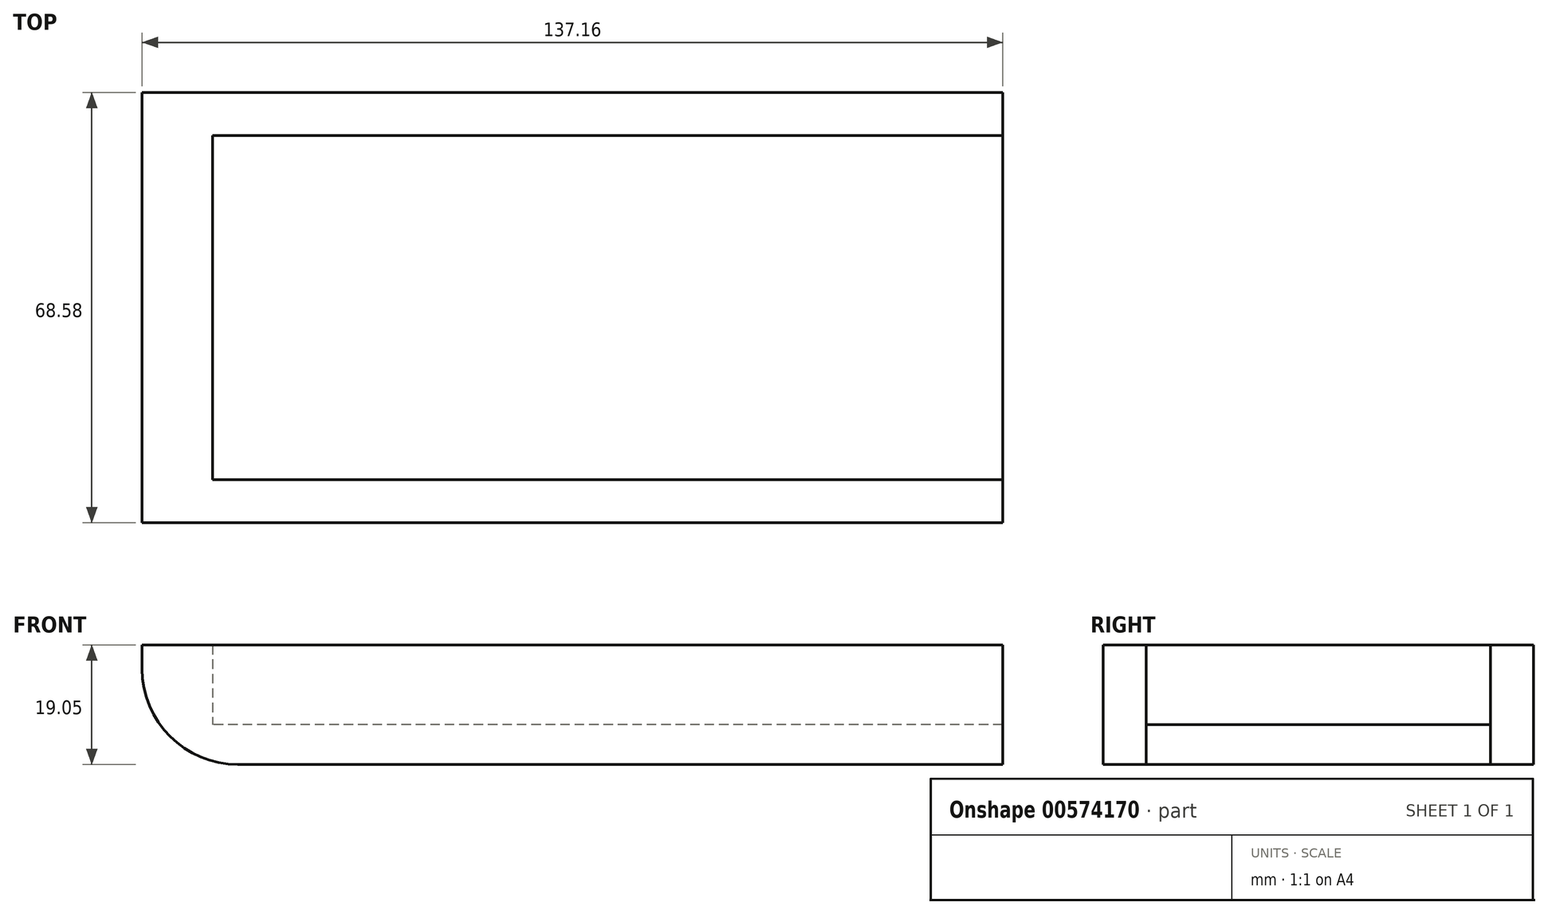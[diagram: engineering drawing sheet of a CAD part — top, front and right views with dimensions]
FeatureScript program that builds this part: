
annotation { "Feature Type Name" : "Feature", "Feature Type Description" : "" }
export const myFeature = defineFeature(function(context is Context, id is Id, definition is map)
    precondition{}
    {
        {
            var Q0;
            Q0=qCreatedBy(makeId("Top.planeOp"),FACE);
            var sketch = newSketch(context, id + "F0", { "sketchPlane" : qUnion([Q0])});
            skLineSegment(sketch, "E0.bottom", {"start": v(-110.64, -23.37) * mm, "end": v(26.52, -23.37) * mm});
            skLineSegment(sketch, "E0.top", {"start": v(-110.64, 45.21) * mm, "end": v(26.52, 45.21) * mm});
            skLineSegment(sketch, "E0.left", {"start": v(-110.64, -23.37) * mm, "end": v(-110.64, 45.21) * mm});
            skLineSegment(sketch, "E0.right", {"start": v(26.52, -23.37) * mm, "end": v(26.52, 45.21) * mm});
            skLineSegment(sketch, "E1.bottom", {"start": v(28.45, 38.35) * mm, "end": v(-99.4, 38.35) * mm});
            skLineSegment(sketch, "E1.top", {"start": v(28.45, -16.52) * mm, "end": v(-99.4, -16.52) * mm});
            skLineSegment(sketch, "E1.left", {"start": v(28.45, 38.35) * mm, "end": v(28.45, -16.52) * mm});
            skLineSegment(sketch, "E1.right", {"start": v(-99.4, 38.35) * mm, "end": v(-99.4, -16.52) * mm});
            skSolve(sketch);
        }
        {
            var Q0;
            {var subQ1=sQuery(id+"F0.wireOp",EDGE,"E0.bottom");Q0=makeQuery(id+"F0.imprint","IMPRINT",FACE,{"disambiguationData":[TD([[makeQuery(id+"F0.imprint","IMPRINT",EDGE,{"derivedFrom":subQ1}),1.0]])]});}
            extrude(context, id + "F1", {"entities" : qUnion([Q0]), "depth" : 19.05 * mm, "offsetDistance" : 25.4 * mm});
        }
        {
            var Q0;
            Q0=qCreatedBy(makeId("Top.planeOp"),FACE);
            var sketch = newSketch(context, id + "F2", { "sketchPlane" : qUnion([Q0])});
            skLineSegment(sketch, "E2.bottom", {"start": v(-101.94, 40.73) * mm, "end": v(26.5, 40.73) * mm});
            skLineSegment(sketch, "E2.top", {"start": v(-101.94, -20.5) * mm, "end": v(26.5, -20.5) * mm});
            skLineSegment(sketch, "E2.left", {"start": v(-101.94, 40.73) * mm, "end": v(-101.94, -20.5) * mm});
            skLineSegment(sketch, "E2.right", {"start": v(26.5, 40.73) * mm, "end": v(26.5, -20.5) * mm});
            skSolve(sketch);
        }
        {
            var Q0;
            Q0 = qSketchRegion(id + "F2", true);
            extrude(context, id + "F3", {"entities" : qUnion([Q0]), "operationType" : NewBodyOperationType.ADD, "depth" : 6.35 * mm, "offsetDistance" : 25.4 * mm});
        }
        {
            var Q0;
            Q0=makeQuery(id+"F1.opExtrude","CAP_EDGE",EDGE,{"disambiguationData":[OSD([sQuery(id+"F0.wireOp",EDGE,"E0.left")])],"isStart":true});
            fillet(context, id + "F4", {"entities" : qUnion([Q0]), "radius" : 15.24 * mm, "tangentPropagation" : true, "allowEdgeOverflow" : false});
        }
    });
